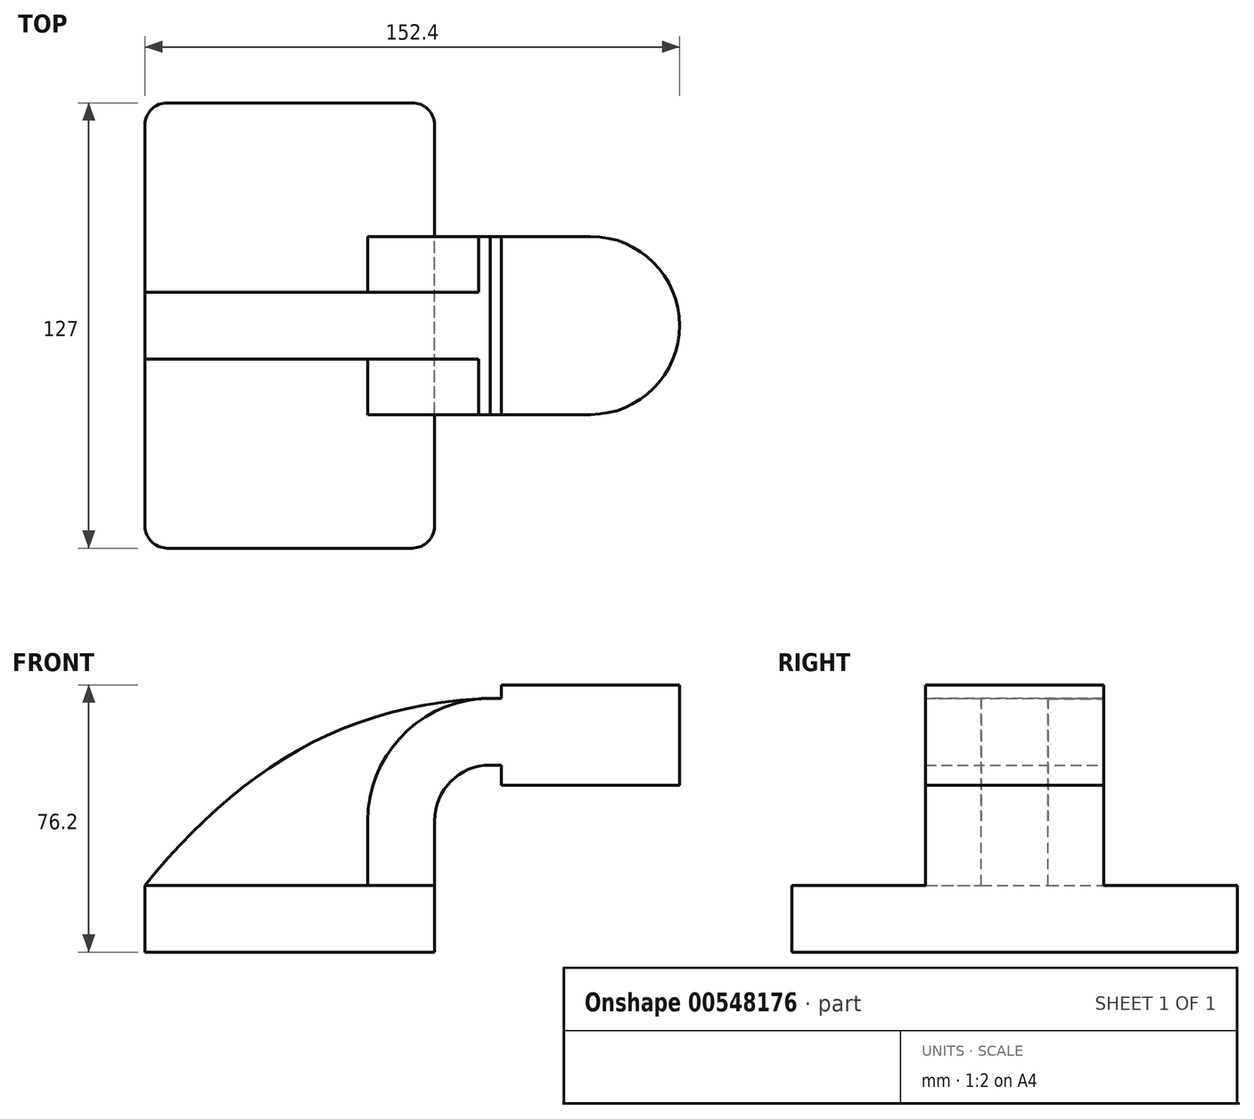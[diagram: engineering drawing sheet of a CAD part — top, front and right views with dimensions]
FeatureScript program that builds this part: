
annotation { "Feature Type Name" : "Feature", "Feature Type Description" : "" }
export const myFeature = defineFeature(function(context is Context, id is Id, definition is map)
    precondition{}
    {
        {
            var Q0;
            Q0=qCreatedBy(makeId("Front.planeOp"),FACE);
            var sketch = newSketch(context, id + "F0", { "sketchPlane" : qUnion([Q0])});
            skLineSegment(sketch, "E0.bottom", {"start": v(-41.28, 9.52) * mm, "end": v(41.27, 9.53) * mm});
            skLineSegment(sketch, "E0.top", {"start": v(-41.28, -9.53) * mm, "end": v(41.28, -9.53) * mm});
            skLineSegment(sketch, "E0.left", {"start": v(-41.28, 9.52) * mm, "end": v(-41.28, -9.53) * mm});
            skLineSegment(sketch, "E0.right", {"start": v(41.27, 9.53) * mm, "end": v(41.28, -9.52) * mm});
            skPoint(sketch, "E0.middle", {"position": v(0, 0) * mm});
            skLineSegment(sketch, "E1.bottom", {"start": v(60.32, 66.68) * mm, "end": v(111.12, 66.68) * mm});
            skLineSegment(sketch, "E1.top", {"start": v(60.32, 38.1) * mm, "end": v(111.12, 38.1) * mm});
            skLineSegment(sketch, "E1.left", {"start": v(60.32, 66.68) * mm, "end": v(60.32, 38.1) * mm});
            skLineSegment(sketch, "E1.right", {"start": v(111.12, 66.68) * mm, "end": v(111.12, 38.1) * mm});
            skPoint(sketch, "E1.middle", {"position": v(85.72, 52.39) * mm});
            skLineSegment(sketch, "E2", {"start": v(41.27, 9.53) * mm, "end": v(41.27, 27.94) * mm});
            skArc(sketch, "E3", {"start": v(41.27, 27.94) * mm, "mid": v(45.92, 39.17) * mm, "end": v(57.15, 43.82) * mm});
            skLineSegment(sketch, "E4", {"start": v(57.15, 43.82) * mm, "end": v(85.72, 43.82) * mm});
            skLineSegment(sketch, "E5.0", {"start": v(57.15, 62.87) * mm, "end": v(85.72, 62.87) * mm});
            skArc(sketch, "E5.1", {"start": v(22.22, 27.94) * mm, "mid": v(32.45, 52.64) * mm, "end": v(57.15, 62.87) * mm});
            skLineSegment(sketch, "E5.2", {"start": v(22.22, 9.53) * mm, "end": v(22.22, 27.94) * mm});
            skLineSegment(sketch, "E6", {"start": v(85.72, 38.1) * mm, "end": v(85.72, 66.68) * mm});
            skFitSpline(sketch, "E7", {"points": [v(-41.28, 9.52) * mm, v(57.15, 62.87) * mm], "startDerivative": vector(77.44, 95.25) * mm, "endDerivative": vector(129.2, 4.66) * mm});
            skSolve(sketch);
        }
        {
            var Q0;
            Q0=makeQuery(id+"F0.imprint","IMPRINT",FACE,{"disambiguationData":[TD([[makeQuery(id+"F0.imprint","IMPRINT",EDGE,{"derivedFrom":sQuery(id+"F0.wireOp",EDGE,"E0.top")}),1.0]])]});
            extrude(context, id + "F1", {"entities" : qUnion([Q0]), "endBound" : BoundingType.SYMMETRIC, "depth" : 127 * mm, "offsetDistance" : 25.4 * mm});
        }
        {
            var Q0;
            {var subQ1=sQuery(id+"F0.wireOp",EDGE,"E2");Q0=makeQuery(id+"F0.imprint","IMPRINT",FACE,{"disambiguationData":[TD([[makeQuery(id+"F0.imprint","IMPRINT",EDGE,{"derivedFrom":subQ1}),1.0]])]});}
            var Q1;
            {var subQ0=sQuery(id+"F0.wireOp",EDGE,"E1.left");var subQ1=sQuery(id+"F0.wireOp",EDGE,"E1.top");var subQ2=makeQuery(id+"F0.imprint","INTERSECT",VERTEX,{"derivedFrom":[subQ1,subQ0]});Q1=makeQuery(id+"F0.imprint","IMPRINT",FACE,{"disambiguationData":[TD([[makeQuery(id+"F0.imprint","IMPRINT",EDGE,{"disambiguationData":[TD([[subQ2,-1.0]])],"derivedFrom":subQ1}),1.0]])]});}
            var Q2;
            {var subQ0=sQuery(id+"F0.wireOp",EDGE,"E1.left");var subQ1=sQuery(id+"F0.wireOp",EDGE,"E1.bottom");var subQ2=makeQuery(id+"F0.imprint","INTERSECT",VERTEX,{"derivedFrom":[subQ1,subQ0]});Q2=makeQuery(id+"F0.imprint","IMPRINT",FACE,{"disambiguationData":[TD([[makeQuery(id+"F0.imprint","IMPRINT",EDGE,{"disambiguationData":[TD([[subQ2,-1.0]])],"derivedFrom":subQ1}),-1.0]])]});}
            var Q3;
            {var subQ0=sQuery(id+"F0.wireOp",EDGE,"E5.0");var subQ1=sQuery(id+"F0.wireOp",EDGE,"E1.left");var subQ2=makeQuery(id+"F0.imprint","INTERSECT",VERTEX,{"derivedFrom":[subQ1,subQ0]});Q3=makeQuery(id+"F0.imprint","IMPRINT",FACE,{"disambiguationData":[TD([[makeQuery(id+"F0.imprint","IMPRINT",EDGE,{"disambiguationData":[TD([[subQ2,-1.0]])],"derivedFrom":subQ1}),1.0]])]});}
            extrude(context, id + "F2", {"entities" : qUnion([Q0, Q1, Q2, Q3]), "operationType" : NewBodyOperationType.ADD, "endBound" : BoundingType.SYMMETRIC, "depth" : 50.8 * mm, "offsetDistance" : 25.4 * mm});
        }
        {
            var Q0;
            {var subQ3=sQuery(id+"F0.wireOp",EDGE,"E5.2");Q0=makeQuery(id+"F0.imprint","IMPRINT",FACE,{"disambiguationData":[TD([[makeQuery(id+"F0.imprint","IMPRINT",EDGE,{"derivedFrom":subQ3}),1.0]])]});}
            extrude(context, id + "F3", {"entities" : qUnion([Q0]), "operationType" : NewBodyOperationType.ADD, "endBound" : BoundingType.SYMMETRIC, "depth" : 19.05 * mm, "offsetDistance" : 25.4 * mm});
        }
        {
            var Q0;
            {var subQ4=sQuery(id+"F0.wireOp",EDGE,"E1.right");Q0=makeQuery(id+"F0.imprint","IMPRINT",FACE,{"disambiguationData":[TD([[makeQuery(id+"F0.imprint","IMPRINT",EDGE,{"derivedFrom":subQ4}),-1.0]])]});}
            var Q1;
            Q1=sQuery(id+"F0.wireOp",EDGE,"E6");
            revolve(context, id + "F4", {"operationType" : NewBodyOperationType.ADD, "entities" : qUnion([Q0]), "axis" : qUnion([Q1]), "revolveType" : RevolveType.FULL});
        }
        {
            var Q0;
            Q0=makeQuery(id+"F1.opExtrude","CAP_EDGE",EDGE,{"disambiguationData":[OSD([sQuery(id+"F0.wireOp",EDGE,"E0.left")])],"isStart":true});
            var Q1;
            Q1=makeQuery(id+"F1.opExtrude","CAP_EDGE",EDGE,{"disambiguationData":[OSD([sQuery(id+"F0.wireOp",EDGE,"E0.right")])],"isStart":true});
            var Q2;
            Q2=makeQuery(id+"F1.opExtrude","CAP_EDGE",EDGE,{"disambiguationData":[OSD([sQuery(id+"F0.wireOp",EDGE,"E0.right")])],"isStart":false});
            var Q3;
            Q3=makeQuery(id+"F1.opExtrude","CAP_EDGE",EDGE,{"disambiguationData":[OSD([sQuery(id+"F0.wireOp",EDGE,"E0.left")])],"isStart":false});
            fillet(context, id + "F5", {"entities" : qUnion([Q0, Q1, Q2, Q3]), "radius" : 6.35 * mm, "tangentPropagation" : true, "allowEdgeOverflow" : false});
        }
    });
